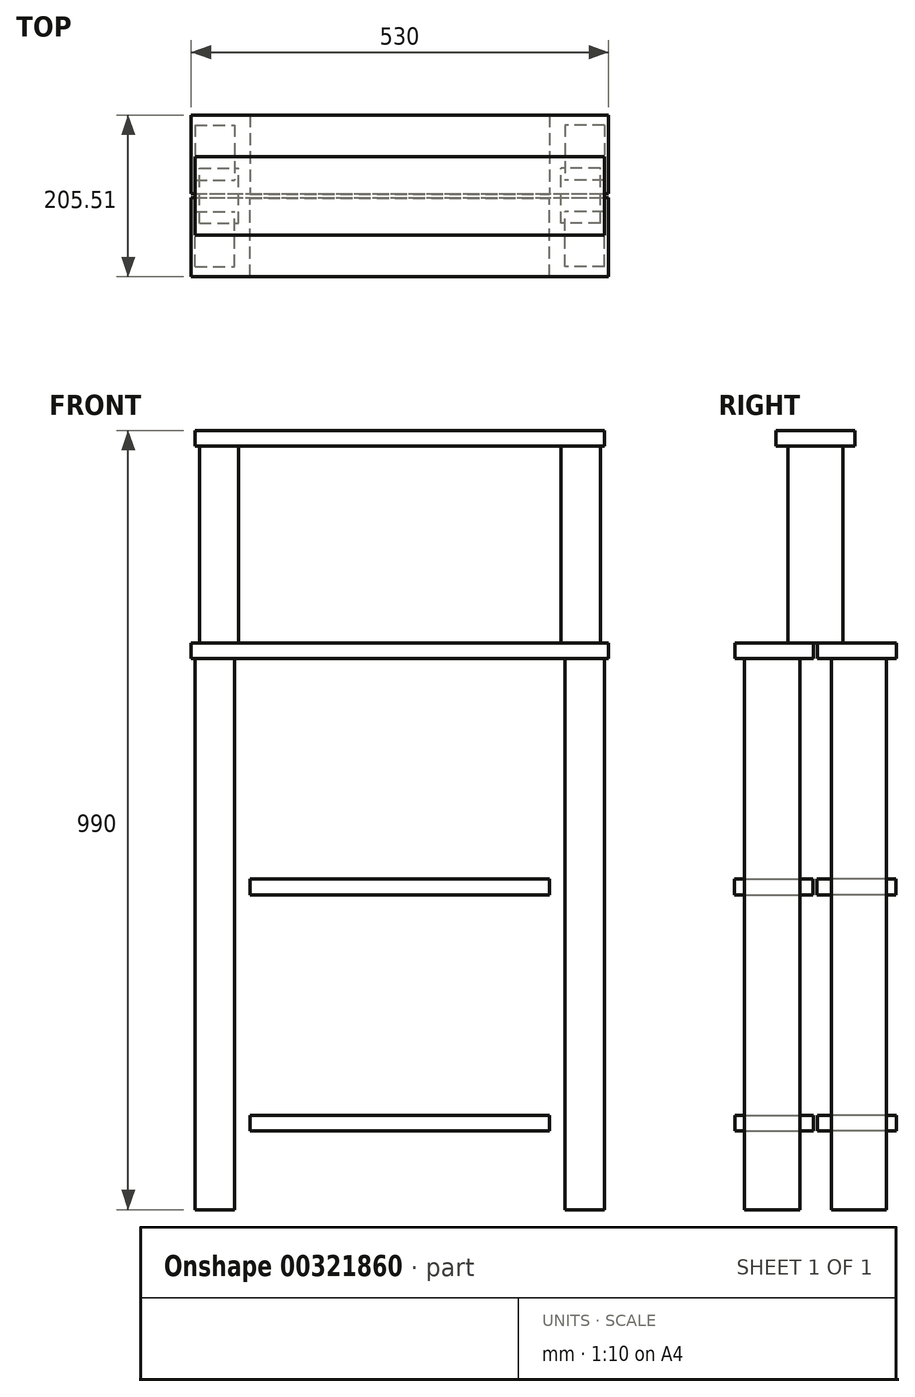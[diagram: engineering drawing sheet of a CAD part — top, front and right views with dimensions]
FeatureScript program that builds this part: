
annotation { "Feature Type Name" : "Feature", "Feature Type Description" : "" }
export const myFeature = defineFeature(function(context is Context, id is Id, definition is map)
    precondition{}
    {
        {
            var Q0;
            Q0=qCreatedBy(makeId("Top.planeOp"),FACE);
            var sketch = newSketch(context, id + "F0", { "sketchPlane" : qUnion([Q0])});
            skLineSegment(sketch, "E0.bottom", {"start": v(-260, -90) * mm, "end": v(-210, -90) * mm});
            skLineSegment(sketch, "E0.top", {"start": v(-260, -20) * mm, "end": v(-210, -20) * mm});
            skLineSegment(sketch, "E0.left", {"start": v(-260, -90) * mm, "end": v(-260, -20) * mm});
            skLineSegment(sketch, "E0.right", {"start": v(-210, -90) * mm, "end": v(-210, -20) * mm});
            skLineSegment(sketch, "E1", {"start": v(-708.75, 0) * mm, "end": v(703.75, 0) * mm, "construction": true});
            skLineSegment(sketch, "E2", {"start": v(0, -508.75) * mm, "end": v(0, 503.75) * mm, "construction": true});
            skLineSegment(sketch, "E3.MirrorCS", {"start": v(-260, 90) * mm, "end": v(-210, 90) * mm});
            skLineSegment(sketch, "E4.MirrorCS", {"start": v(-260, 20) * mm, "end": v(-210, 20) * mm});
            skLineSegment(sketch, "E5.MirrorCS", {"start": v(-210, 90) * mm, "end": v(-210, 20) * mm});
            skLineSegment(sketch, "E6.MirrorCS", {"start": v(-260, 90) * mm, "end": v(-260, 20) * mm});
            skLineSegment(sketch, "E7.MirrorCS", {"start": v(260, 90) * mm, "end": v(260, 20) * mm});
            skLineSegment(sketch, "E8.MirrorCS", {"start": v(210, 90) * mm, "end": v(210, 20) * mm});
            skLineSegment(sketch, "E9.MirrorCS", {"start": v(260, 20) * mm, "end": v(210, 20) * mm});
            skLineSegment(sketch, "E10.MirrorCS", {"start": v(260, 90) * mm, "end": v(210, 90) * mm});
            skLineSegment(sketch, "E11.MirrorCS", {"start": v(260, -90) * mm, "end": v(210, -90) * mm});
            skLineSegment(sketch, "E12.MirrorCS", {"start": v(260, -20) * mm, "end": v(210, -20) * mm});
            skLineSegment(sketch, "E13.MirrorCS", {"start": v(260, -90) * mm, "end": v(260, -20) * mm});
            skLineSegment(sketch, "E14.MirrorCS", {"start": v(210, -90) * mm, "end": v(210, -20) * mm});
            skSolve(sketch);
        }
        {
            var Q0;
            Q0 = qSketchRegion(id + "F0", true);
            extrude(context, id + "F1", {"entities" : qUnion([Q0]), "depth" : 700 * mm, "offsetDistance" : 25 * mm});
        }
        {
            var Q0;
            Q0=makeQuery(id+"F1.opExtrude","CAP_FACE",FACE,{"disambiguationData":[OSD([sQuery(id+"F0.wireOp",EDGE,"E0.bottom"),sQuery(id+"F0.wireOp",EDGE,"E0.top"),sQuery(id+"F0.wireOp",EDGE,"E0.left"),sQuery(id+"F0.wireOp",EDGE,"E0.right")])],"isStart":false});
            var sketch = newSketch(context, id + "F2", { "sketchPlane" : qUnion([Q0])});
            skLineSegment(sketch, "E15", {"start": v(0, -66.9) * mm, "end": v(0, 103.28) * mm, "construction": true});
            skLineSegment(sketch, "E16", {"start": v(-176.69, 0) * mm, "end": v(242.27, 0) * mm, "construction": true});
            skLineSegment(sketch, "E17.bottom", {"start": v(-265, -102.5) * mm, "end": v(265, -102.5) * mm});
            skLineSegment(sketch, "E17.top", {"start": v(-265, -2.5) * mm, "end": v(265, -2.5) * mm});
            skLineSegment(sketch, "E17.left", {"start": v(-265, -102.5) * mm, "end": v(-265, -2.5) * mm});
            skLineSegment(sketch, "E17.right", {"start": v(265, -102.5) * mm, "end": v(265, -2.5) * mm});
            skLineSegment(sketch, "E18.MirrorCS", {"start": v(-265, 102.5) * mm, "end": v(-265, 2.5) * mm});
            skLineSegment(sketch, "E19.MirrorCS", {"start": v(-265, 102.5) * mm, "end": v(265, 102.5) * mm});
            skLineSegment(sketch, "E20.MirrorCS", {"start": v(-265, 2.5) * mm, "end": v(265, 2.5) * mm});
            skLineSegment(sketch, "E21.MirrorCS", {"start": v(265, 102.5) * mm, "end": v(265, 2.5) * mm});
            skSolve(sketch);
        }
        {
            var Q0;
            Q0 = qSketchRegion(id + "F2", true);
            extrude(context, id + "F3", {"entities" : qUnion([Q0]), "depth" : 20 * mm, "offsetDistance" : 25 * mm});
        }
        {
            var Q0;
            Q0=qCreatedBy(makeId("Top.planeOp"),FACE);
            cPlane(context, id + "F4", {"entities" : qUnion([Q0]), "cplaneType" : CPlaneType.OFFSET, "offset" : 100 * mm, "width" : 150 * mm, "height" : 150 * mm});
        }
        {
            var Q0;
            Q0=qCreatedBy(id+"F4.planeOp",FACE);
            var sketch = newSketch(context, id + "F5", { "sketchPlane" : qUnion([Q0])});
            skLineSegment(sketch, "E22", {"start": v(0, -110.32) * mm, "end": v(0, 120.52) * mm, "construction": true});
            skLineSegment(sketch, "E23", {"start": v(-309.12, 0) * mm, "end": v(309.55, 0) * mm, "construction": true});
            skLineSegment(sketch, "E24.bottom", {"start": v(-190.06, -102.5) * mm, "end": v(190.06, -102.5) * mm});
            skLineSegment(sketch, "E24.top", {"start": v(-190.06, -2.5) * mm, "end": v(190.06, -2.5) * mm});
            skLineSegment(sketch, "E24.left", {"start": v(-190.06, -102.5) * mm, "end": v(-190.06, -2.5) * mm});
            skLineSegment(sketch, "E24.right", {"start": v(190.06, -102.5) * mm, "end": v(190.06, -2.5) * mm});
            skLineSegment(sketch, "E25.MirrorCS", {"start": v(-190.06, 102.5) * mm, "end": v(190.06, 102.5) * mm});
            skLineSegment(sketch, "E26.MirrorCS", {"start": v(-190.06, 2.5) * mm, "end": v(190.06, 2.5) * mm});
            skLineSegment(sketch, "E27.MirrorCS", {"start": v(190.06, 102.5) * mm, "end": v(190.06, 2.5) * mm});
            skLineSegment(sketch, "E28.MirrorCS", {"start": v(-190.06, 102.5) * mm, "end": v(-190.06, 2.5) * mm});
            skSolve(sketch);
        }
        {
            var Q0;
            Q0 = qSketchRegion(id + "F5", true);
            extrude(context, id + "F6", {"entities" : qUnion([Q0]), "depth" : 20 * mm, "offsetDistance" : 25 * mm});
        }
        {
            var Q0;
            Q0=makeQuery(id+"F3.opExtrude","CAP_FACE",FACE,{"disambiguationData":[OSD([sQuery(id+"F2.wireOp",EDGE,"E17.bottom"),sQuery(id+"F2.wireOp",EDGE,"E17.top"),sQuery(id+"F2.wireOp",EDGE,"E17.left"),sQuery(id+"F2.wireOp",EDGE,"E17.right")])],"isStart":false});
            var sketch = newSketch(context, id + "F7", { "sketchPlane" : qUnion([Q0])});
            skLineSegment(sketch, "E29", {"start": v(0, -102.5) * mm, "end": v(0, 104.65) * mm, "construction": true});
            skLineSegment(sketch, "E30.bottom", {"start": v(-254.62, -35) * mm, "end": v(-204.62, -35) * mm});
            skLineSegment(sketch, "E30.top", {"start": v(-254.62, 35) * mm, "end": v(-204.62, 35) * mm});
            skLineSegment(sketch, "E30.left", {"start": v(-254.62, -35) * mm, "end": v(-254.62, 35) * mm});
            skLineSegment(sketch, "E30.right", {"start": v(-204.62, -35) * mm, "end": v(-204.62, 35) * mm});
            skLineSegment(sketch, "E31", {"start": v(-293.73, 0) * mm, "end": v(326.85, 0) * mm, "construction": true});
            skLineSegment(sketch, "E32.MirrorCS", {"start": v(254.62, -35) * mm, "end": v(204.62, -35) * mm});
            skLineSegment(sketch, "E33.MirrorCS", {"start": v(254.62, 35) * mm, "end": v(204.62, 35) * mm});
            skLineSegment(sketch, "E34.MirrorCS", {"start": v(254.62, -35) * mm, "end": v(254.62, 35) * mm});
            skLineSegment(sketch, "E35.MirrorCS", {"start": v(204.62, -35) * mm, "end": v(204.62, 35) * mm});
            skSolve(sketch);
        }
        {
            var Q0;
            Q0 = qSketchRegion(id + "F7", true);
            extrude(context, id + "F8", {"entities" : qUnion([Q0]), "depth" : 250 * mm, "offsetDistance" : 25 * mm});
        }
        {
            var Q0;
            Q0=makeQuery(id+"F8.opExtrude","CAP_FACE",FACE,{"disambiguationData":[OSD([sQuery(id+"F7.wireOp",EDGE,"E30.bottom"),sQuery(id+"F7.wireOp",EDGE,"E30.top"),sQuery(id+"F7.wireOp",EDGE,"E30.left"),sQuery(id+"F7.wireOp",EDGE,"E30.right")])],"isStart":false});
            var sketch = newSketch(context, id + "F9", { "sketchPlane" : qUnion([Q0])});
            skLineSegment(sketch, "E36", {"start": v(0, -80.66) * mm, "end": v(0, 83.65) * mm, "construction": true});
            skLineSegment(sketch, "E37.bottom", {"start": v(-260, -50) * mm, "end": v(260, -50) * mm});
            skLineSegment(sketch, "E37.top", {"start": v(-260, 50) * mm, "end": v(260, 50) * mm});
            skLineSegment(sketch, "E37.left", {"start": v(-260, -50) * mm, "end": v(-260, 50) * mm});
            skLineSegment(sketch, "E37.right", {"start": v(260, -50) * mm, "end": v(260, 50) * mm});
            skLineSegment(sketch, "E38", {"start": v(-223.5, 0) * mm, "end": v(241.14, 0) * mm, "construction": true});
            skSolve(sketch);
        }
        {
            var Q0;
            Q0 = qSketchRegion(id + "F9", true);
            extrude(context, id + "F10", {"entities" : qUnion([Q0]), "depth" : 20 * mm, "offsetDistance" : 25 * mm});
        }
        {
            var Q0;
            Q0=qCreatedBy(makeId("Top.planeOp"),FACE);
            cPlane(context, id + "F11", {"entities" : qUnion([Q0]), "cplaneType" : CPlaneType.OFFSET, "offset" : 400 * mm, "width" : 150 * mm, "height" : 150 * mm});
        }
        {
            var Q0;
            Q0=qCreatedBy(id+"F11.planeOp",FACE);
            var sketch = newSketch(context, id + "F12", { "sketchPlane" : qUnion([Q0])});
            skLineSegment(sketch, "E39", {"start": v(-0.02, -110.83) * mm, "end": v(-0.02, 120) * mm, "construction": true});
            skLineSegment(sketch, "E40", {"start": v(-309.14, -0.5) * mm, "end": v(309.52, -0.5) * mm, "construction": true});
            skLineSegment(sketch, "E41.bottom", {"start": v(-190.08, -103) * mm, "end": v(190.04, -103) * mm});
            skLineSegment(sketch, "E41.top", {"start": v(-190.08, -3) * mm, "end": v(190.04, -3) * mm});
            skLineSegment(sketch, "E41.left", {"start": v(-190.08, -103) * mm, "end": v(-190.08, -3) * mm});
            skLineSegment(sketch, "E41.right", {"start": v(190.04, -103) * mm, "end": v(190.04, -3) * mm});
            skLineSegment(sketch, "E42.MirrorCS", {"start": v(-190.08, 102) * mm, "end": v(190.04, 102) * mm});
            skLineSegment(sketch, "E43.MirrorCS", {"start": v(-190.08, 2) * mm, "end": v(190.04, 2) * mm});
            skLineSegment(sketch, "E44.MirrorCS", {"start": v(190.04, 102) * mm, "end": v(190.04, 2) * mm});
            skLineSegment(sketch, "E45.MirrorCS", {"start": v(-190.08, 102) * mm, "end": v(-190.08, 2) * mm});
            skSolve(sketch);
        }
        {
            var Q0;
            Q0 = qSketchRegion(id + "F12", true);
            extrude(context, id + "F13", {"entities" : qUnion([Q0]), "depth" : 20 * mm, "offsetDistance" : 25 * mm});
        }
    });
